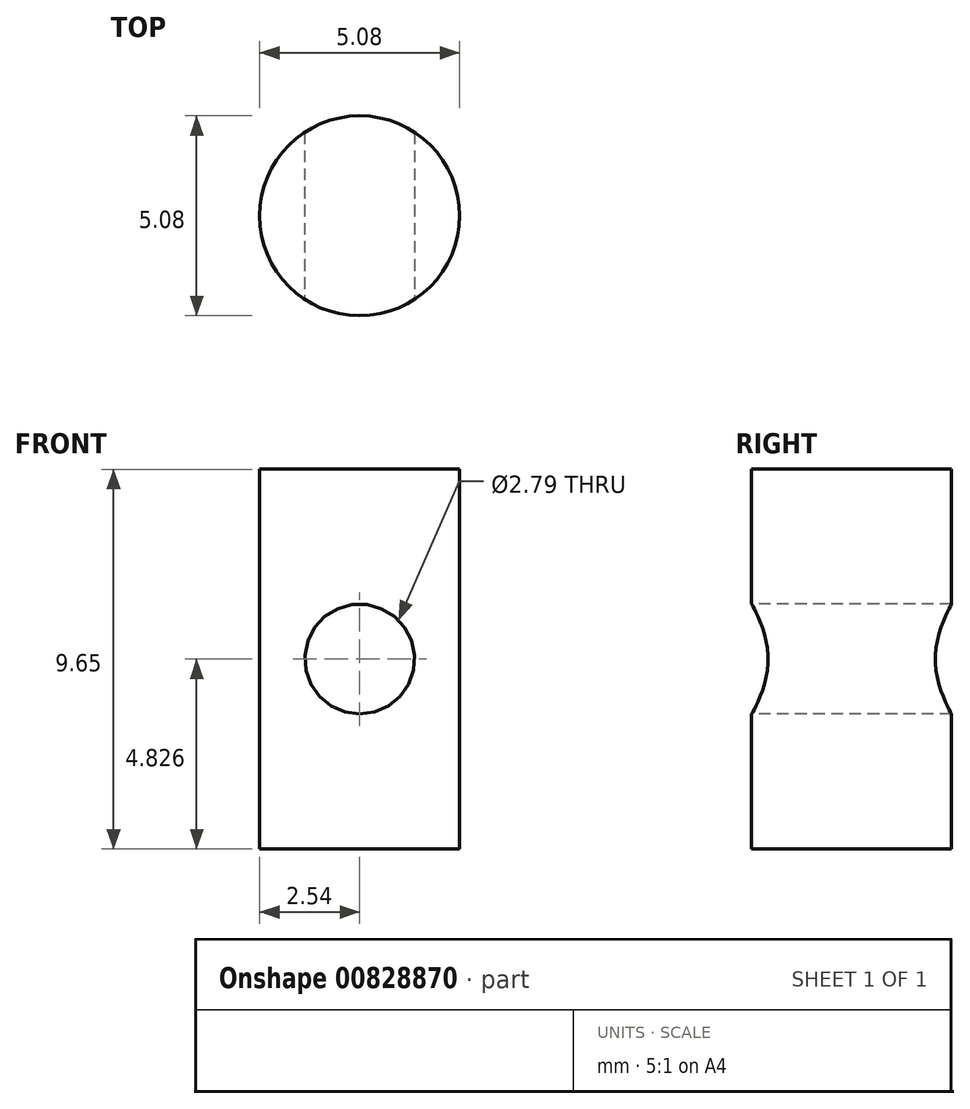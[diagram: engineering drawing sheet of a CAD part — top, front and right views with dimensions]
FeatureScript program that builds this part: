
annotation { "Feature Type Name" : "Feature", "Feature Type Description" : "" }
export const myFeature = defineFeature(function(context is Context, id is Id, definition is map)
    precondition{}
    {
        {
            var Q0;
            Q0=qCreatedBy(makeId("Top.planeOp"),FACE);
            var sketch = newSketch(context, id + "F0", { "sketchPlane" : qUnion([Q0])});
            skCircle(sketch, "E0", {"center": v(0, 0) * mm, "radius": 2.54 * mm});
            skSolve(sketch);
        }
        {
            var Q0;
            Q0 = qSketchRegion(id + "F0", true);
            extrude(context, id + "F1", {"entities" : qUnion([Q0]), "depth" : 9.65 * mm, "offsetDistance" : 25.4 * mm});
        }
        {
            var Q0;
            Q0=qCreatedBy(makeId("Front.planeOp"),FACE);
            var sketch = newSketch(context, id + "F2", { "sketchPlane" : qUnion([Q0])});
            skLineSegment(sketch, "E1", {"start": v(0, 0) * mm, "end": v(0, 9.65) * mm, "construction": true});
            skCircle(sketch, "E2", {"center": v(0, 4.83) * mm, "radius": 1.4 * mm});
            skSolve(sketch);
        }
        {
            var Q0;
            Q0 = qSketchRegion(id + "F2", true);
            extrude(context, id + "F3", {"entities" : qUnion([Q0]), "operationType" : NewBodyOperationType.REMOVE, "oppositeDirection" : true, "depth" : 25.4 * mm, "offsetDistance" : 25.4 * mm, "symmetric" : true});
        }
    });
